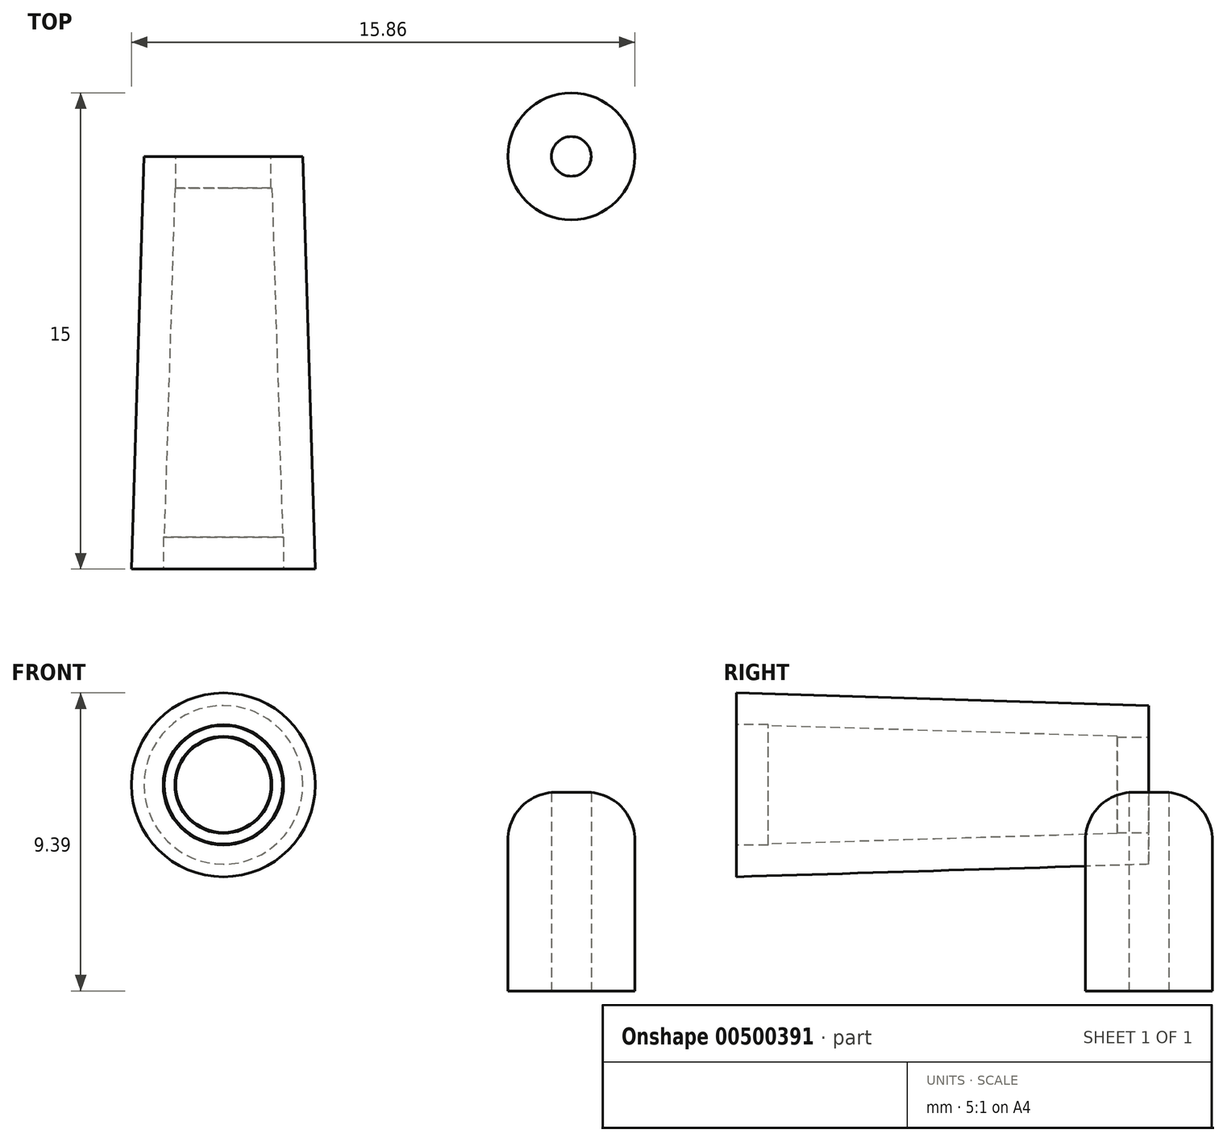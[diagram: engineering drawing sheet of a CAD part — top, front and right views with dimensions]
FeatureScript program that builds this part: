
annotation { "Feature Type Name" : "Feature", "Feature Type Description" : "" }
export const myFeature = defineFeature(function(context is Context, id is Id, definition is map)
    precondition{}
    {
        {
            var Q0;
            Q0=qCreatedBy(makeId("Top.planeOp"),FACE);
            var sketch = newSketch(context, id + "F0", { "sketchPlane" : qUnion([Q0])});
            skCircle(sketch, "E0", {"center": v(0, 0) * mm, "radius": 2 * mm});
            skCircle(sketch, "E1", {"center": v(0, 0) * mm, "radius": 0.62 * mm});
            skSolve(sketch);
        }
        {
            var Q0;
            Q0=qSketchRegion(id+"F0",true);
            extrude(context, id + "F1", {"entities" : qUnion([Q0]), "depth" : 6.25 * mm});
        }
        {
            var Q0;
            Q0=makeQuery(id+"F1.opExtrude","CAP_EDGE",EDGE,{"disambiguationData":[OSD([sQuery(id+"F0.wireOp",EDGE,"E0")])],"isStart":false});
            fillet(context, id + "F2", {"entities" : qUnion([Q0]), "radius" : 1.5 * mm, "tangentPropagation" : true, "allowEdgeOverflow" : false});
        }
        {
            var Q0;
            Q0=qCreatedBy(makeId("Front.planeOp"),FACE);
            var sketch = newSketch(context, id + "F3", { "sketchPlane" : qUnion([Q0])});
            skCircle(sketch, "E2", {"center": v(-10.97, 6.5) * mm, "radius": 2.5 * mm});
            skSolve(sketch);
        }
        {
            var Q0;
            Q0=qSketchRegion(id+"F3",true);
            extrude(context, id + "F4", {"entities" : qUnion([Q0]), "depth" : 13 * mm, "hasDraft" : true, "draftAngle" : 1.75 * degree});
        }
        {
            var Q0;
            Q0=makeQuery(id+"F4.opExtrude","CAP_FACE",FACE,{"disambiguationData":[OSD([sQuery(id+"F3.wireOp",EDGE,"E2")])],"isStart":false});
            var sketch = newSketch(context, id + "F5", { "sketchPlane" : qUnion([Q0])});
            skCircle(sketch, "E3", {"center": v(-10.97, 6.5) * mm, "radius": 2.9 * mm});
            skCircle(sketch, "E4", {"center": v(-10.97, 6.5) * mm, "radius": 1.9 * mm});
            skSolve(sketch);
        }
        {
            var Q0;
            Q0=makeQuery(id+"F4.opExtrude","CAP_FACE",FACE,{"disambiguationData":[OSD([sQuery(id+"F3.wireOp",EDGE,"E2")])],"isStart":false});
            var Q1;
            Q1=makeQuery(id+"F4.opExtrude","SWEPT_BODY",BODY,{"disambiguationData":[OSD([sQuery(id+"F3.wireOp",EDGE,"E2")])]});
            shell(context, id + "F6", {"isHollow" : true, "entities" : qUnion([Q0]), "parts" : qUnion([Q1]), "thickness" : 1 * mm});
        }
        {
            var Q0;
            Q0=makeQuery(id+"F5.imprint","IMPRINT",FACE,{"disambiguationData":[TD([[makeQuery(id+"F5.imprint","IMPRINT",EDGE,{"derivedFrom":sQuery(id+"F5.wireOp",EDGE,"E4")}),1.0]])]});
            extrude(context, id + "F7", {"entities" : qUnion([Q0]), "operationType" : NewBodyOperationType.REMOVE, "oppositeDirection" : true, "depth" : 1 * mm});
        }
        {
            var Q0;
            Q0=makeQuery(id+"F4.opExtrude","CAP_FACE",FACE,{"disambiguationData":[OSD([sQuery(id+"F3.wireOp",EDGE,"E2")])],"isStart":true});
            var sketch = newSketch(context, id + "F8", { "sketchPlane" : qUnion([Q0])});
            skCircle(sketch, "E5", {"center": v(10.97, 6.5) * mm, "radius": 1.5 * mm});
            skSolve(sketch);
        }
        {
            var Q0;
            Q0=qSketchRegion(id+"F8",true);
            extrude(context, id + "F9", {"entities" : qUnion([Q0]), "operationType" : NewBodyOperationType.REMOVE, "oppositeDirection" : true, "depth" : 1 * mm});
        }
    });
